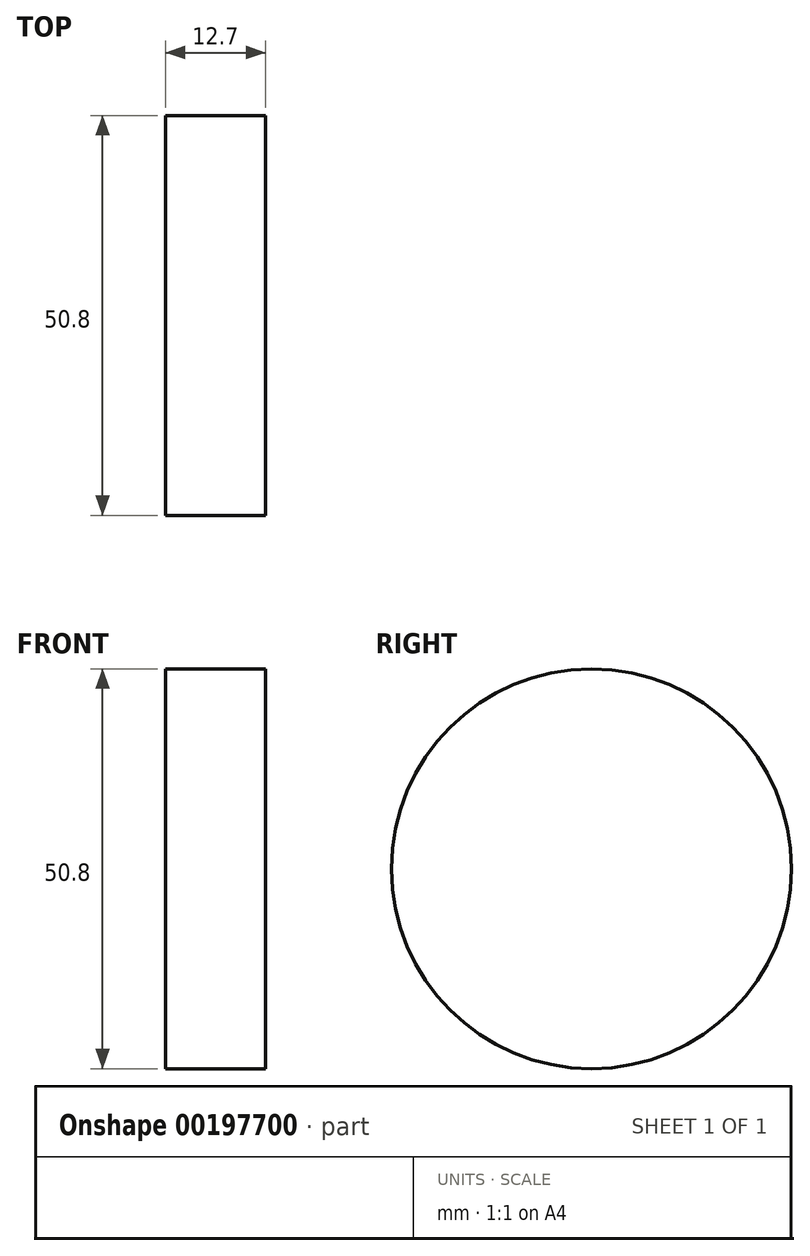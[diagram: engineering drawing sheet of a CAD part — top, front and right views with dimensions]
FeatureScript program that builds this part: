
annotation { "Feature Type Name" : "Feature", "Feature Type Description" : "" }
export const myFeature = defineFeature(function(context is Context, id is Id, definition is map)
    precondition{}
    {
        {
            var Q0;
            Q0=qCreatedBy(makeId("Right.planeOp"),FACE);
            var sketch = newSketch(context, id + "F0", { "sketchPlane" : qUnion([Q0])});
            skCircle(sketch, "E0", {"center": v(0, 0) * mm, "radius": 25.4 * mm});
            skSolve(sketch);
        }
        {
            var Q0;
            Q0 = qSketchRegion(id + "F0", true);
            extrude(context, id + "F1", {"entities" : qUnion([Q0]), "depth" : 12.7 * mm});
        }
    });
